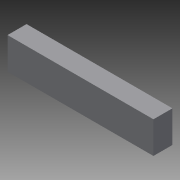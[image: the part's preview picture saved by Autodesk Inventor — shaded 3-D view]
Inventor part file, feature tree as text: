
AUTODESK INVENTOR PART (.ipt)
format: ipt  version: 2013 (Build 170138000, 138)  size: 70,144 bytes
history: native  units: in
note: dims shown in document units (in); Inventor stores cm internally (conversion verified against a paired STEP export)
features: extrude x1, sketch x1
ambient origin geometry x8: Origin, YZ Plane, XZ Plane, XY Plane, X Axis, Y Axis, Z Axis, Center Point
bodies: Solid1 (feature_tree)
feature tree (2):
  extrude  "Extrusion1"  Depth=4.0in
  sketch  "Sketch1"  dims[d0=3.625in d1=4.0in d2=5.0in d3=23.0in d4=5.0in d5=3.0in d6=0.0in]
